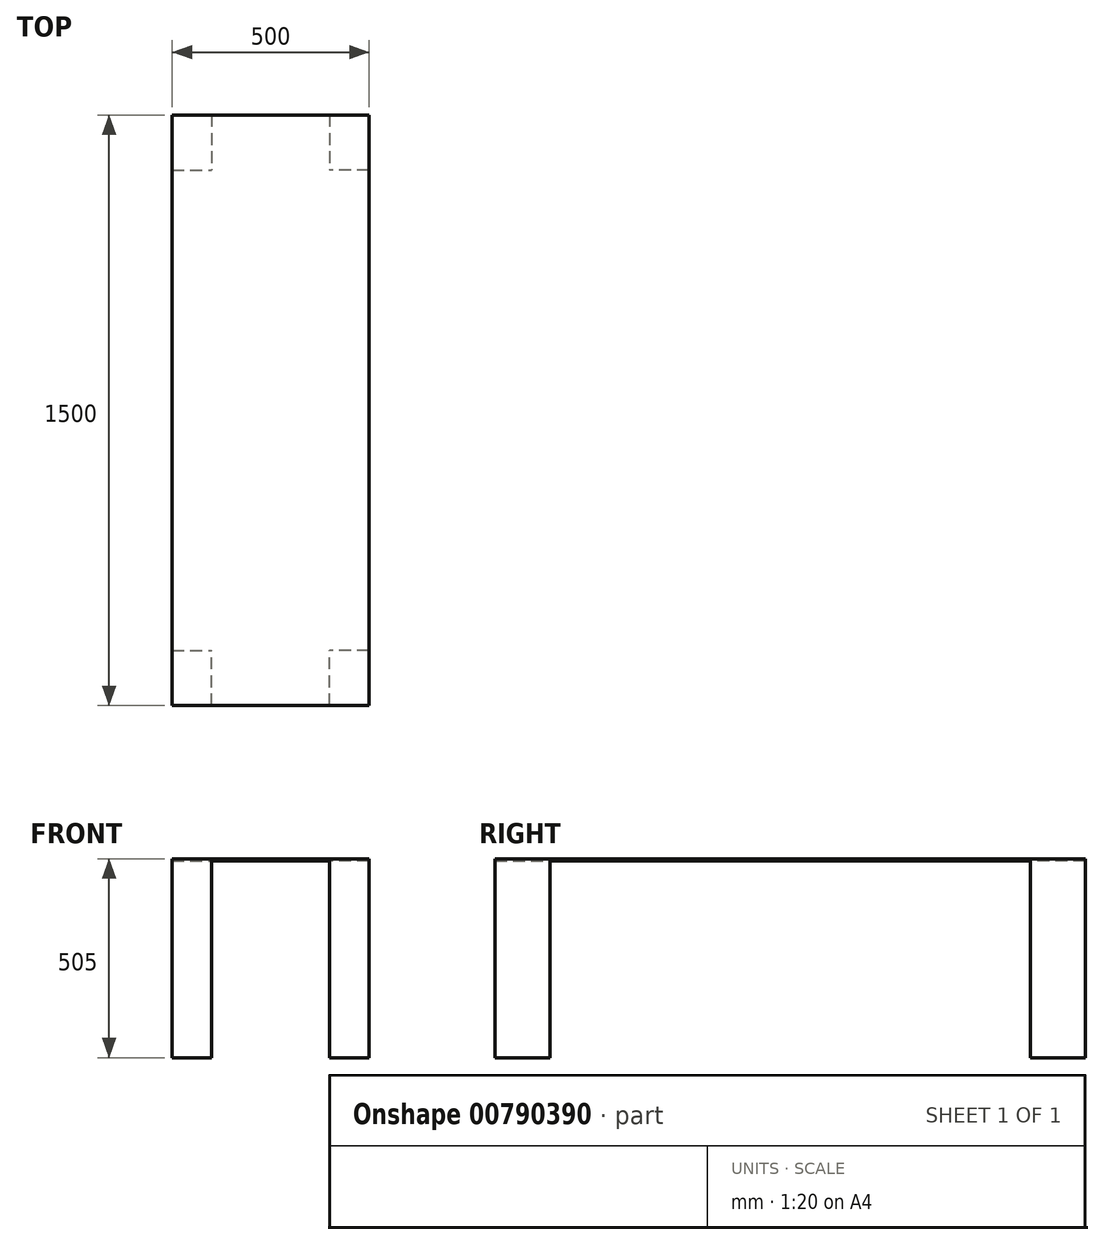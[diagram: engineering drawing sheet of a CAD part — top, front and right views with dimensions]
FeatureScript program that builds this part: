
annotation { "Feature Type Name" : "Feature", "Feature Type Description" : "" }
export const myFeature = defineFeature(function(context is Context, id is Id, definition is map)
    precondition{}
    {
        {
            var Q0;
            Q0=qCreatedBy(makeId("Top.planeOp"),FACE);
            var sketch = newSketch(context, id + "F0", { "sketchPlane" : qUnion([Q0])});
            skLineSegment(sketch, "E0.bottom", {"start": v(250, -750) * mm, "end": v(-250, -750) * mm});
            skLineSegment(sketch, "E0.top", {"start": v(250, 750) * mm, "end": v(-250, 750) * mm});
            skLineSegment(sketch, "E0.left", {"start": v(250, -750) * mm, "end": v(250, 750) * mm});
            skLineSegment(sketch, "E0.right", {"start": v(-250, -750) * mm, "end": v(-250, 750) * mm});
            skPoint(sketch, "E0.middle", {"position": v(0, 0) * mm});
            skSolve(sketch);
        }
        {
            var Q0;
            Q0=makeQuery(id+"F0.imprint","IMPRINT",FACE,{"disambiguationData":[TD([[makeQuery(id+"F0.imprint","IMPRINT",EDGE,{"derivedFrom":sQuery(id+"F0.wireOp",EDGE,"E0.bottom")}),-1.0]])]});
            extrude(context, id + "F1", {"entities" : qUnion([Q0]), "depth" : 5 * mm, "offsetDistance" : 25 * mm});
        }
        {
            var Q0;
            Q0=makeQuery(id+"F1.opExtrude","CAP_FACE",FACE,{"disambiguationData":[OSD([sQuery(id+"F0.wireOp",EDGE,"E0.bottom"),sQuery(id+"F0.wireOp",EDGE,"E0.top"),sQuery(id+"F0.wireOp",EDGE,"E0.left"),sQuery(id+"F0.wireOp",EDGE,"E0.right")])],"isStart":true});
            var sketch = newSketch(context, id + "F2", { "sketchPlane" : qUnion([Q0])});
            skLineSegment(sketch, "E1.bottom", {"start": v(-250, 750) * mm, "end": v(-150, 750) * mm});
            skLineSegment(sketch, "E1.top", {"start": v(-250, 610) * mm, "end": v(-150, 610) * mm});
            skLineSegment(sketch, "E1.left", {"start": v(-250, 750) * mm, "end": v(-250, 610) * mm});
            skLineSegment(sketch, "E1.right", {"start": v(-150, 750) * mm, "end": v(-150, 610) * mm});
            skLineSegment(sketch, "E2.bottom", {"start": v(250, 750) * mm, "end": v(150, 750) * mm});
            skLineSegment(sketch, "E2.top", {"start": v(250, 610) * mm, "end": v(150, 610) * mm});
            skLineSegment(sketch, "E2.left", {"start": v(250, 750) * mm, "end": v(250, 610) * mm});
            skLineSegment(sketch, "E2.right", {"start": v(150, 750) * mm, "end": v(150, 610) * mm});
            skLineSegment(sketch, "E3.bottom", {"start": v(-250, -750) * mm, "end": v(-150, -750) * mm});
            skLineSegment(sketch, "E3.top", {"start": v(-250, -610) * mm, "end": v(-150, -610) * mm});
            skLineSegment(sketch, "E3.left", {"start": v(-250, -750) * mm, "end": v(-250, -610) * mm});
            skLineSegment(sketch, "E3.right", {"start": v(-150, -750) * mm, "end": v(-150, -610) * mm});
            skLineSegment(sketch, "E4.bottom", {"start": v(250, -750) * mm, "end": v(150, -750) * mm});
            skLineSegment(sketch, "E4.top", {"start": v(250, -610) * mm, "end": v(150, -610) * mm});
            skLineSegment(sketch, "E4.left", {"start": v(250, -750) * mm, "end": v(250, -610) * mm});
            skLineSegment(sketch, "E4.right", {"start": v(150, -750) * mm, "end": v(150, -610) * mm});
            skSolve(sketch);
        }
        {
            var Q0;
            Q0=makeQuery(id+"F2.imprint","IMPRINT",FACE,{"disambiguationData":[TD([[makeQuery(id+"F2.imprint","IMPRINT",EDGE,{"derivedFrom":sQuery(id+"F2.wireOp",EDGE,"E1.bottom")}),1.0]])]});
            var Q1;
            Q1=makeQuery(id+"F2.imprint","IMPRINT",FACE,{"disambiguationData":[TD([[makeQuery(id+"F2.imprint","IMPRINT",EDGE,{"derivedFrom":sQuery(id+"F2.wireOp",EDGE,"E2.bottom")}),1.0]])]});
            var Q2;
            Q2=makeQuery(id+"F2.imprint","IMPRINT",FACE,{"disambiguationData":[TD([[makeQuery(id+"F2.imprint","IMPRINT",EDGE,{"derivedFrom":sQuery(id+"F2.wireOp",EDGE,"E4.bottom")}),-1.0]])]});
            var Q3;
            Q3=makeQuery(id+"F2.imprint","IMPRINT",FACE,{"disambiguationData":[TD([[makeQuery(id+"F2.imprint","IMPRINT",EDGE,{"derivedFrom":sQuery(id+"F2.wireOp",EDGE,"E3.bottom")}),-1.0]])]});
            extrude(context, id + "F3", {"entities" : qUnion([Q0, Q1, Q2, Q3]), "operationType" : NewBodyOperationType.ADD, "depth" : 500 * mm, "offsetDistance" : 25 * mm});
        }
    });
